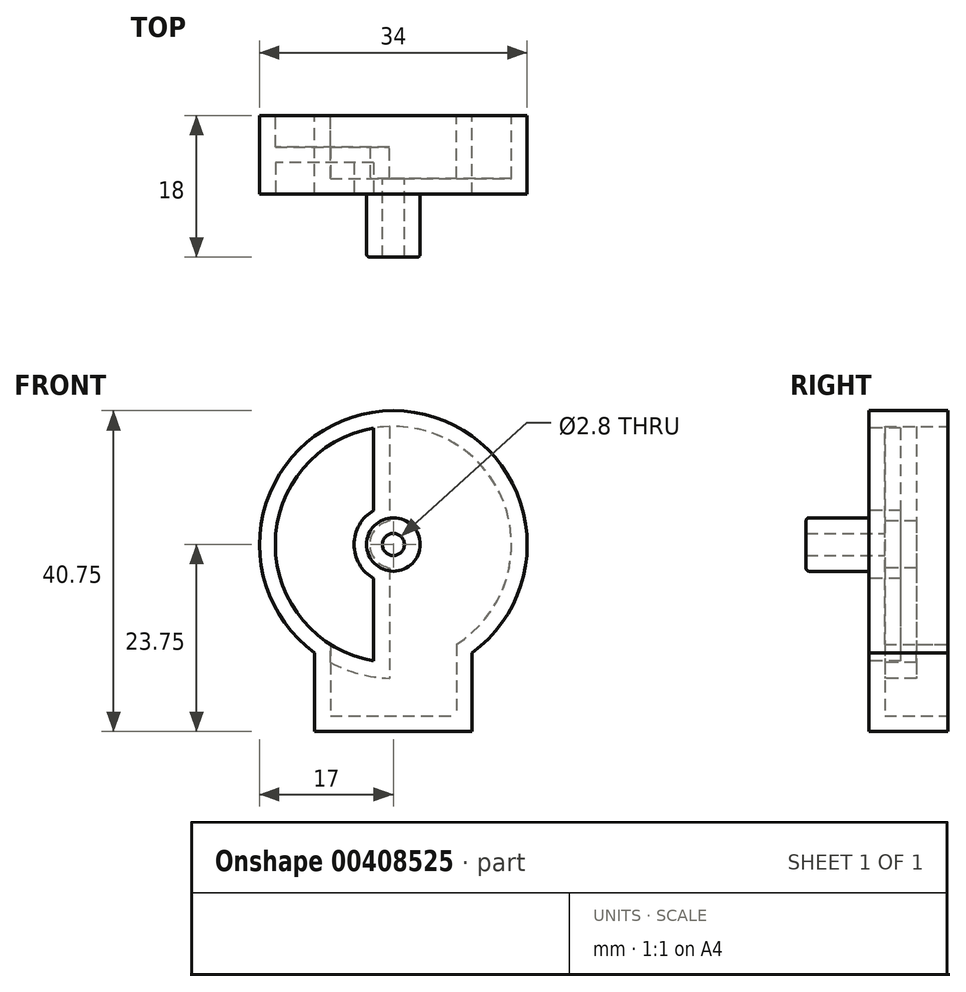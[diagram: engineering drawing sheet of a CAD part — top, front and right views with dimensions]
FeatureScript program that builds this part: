
annotation { "Feature Type Name" : "Feature", "Feature Type Description" : "" }
export const myFeature = defineFeature(function(context is Context, id is Id, definition is map)
    precondition{}
    {
        {
            var Q0;
            Q0=qCreatedBy(makeId("Front.planeOp"),FACE);
            var sketch = newSketch(context, id + "F0", { "sketchPlane" : qUnion([Q0])});
            skCircle(sketch, "E0", {"center": v(0, 0) * mm, "radius": 17 * mm});
            skLineSegment(sketch, "E1.bottom", {"start": v(-10, -13.75) * mm, "end": v(10, -13.75) * mm, "construction": true});
            skLineSegment(sketch, "E1.top", {"start": v(-10, -23.75) * mm, "end": v(10, -23.75) * mm});
            skLineSegment(sketch, "E1.left", {"start": v(-10, -13.75) * mm, "end": v(-10, -23.75) * mm});
            skLineSegment(sketch, "E1.right", {"start": v(10, -13.75) * mm, "end": v(10, -23.75) * mm});
            skLineSegment(sketch, "E2", {"start": v(0, 0) * mm, "end": v(0, -23.75) * mm, "construction": true});
            skPoint(sketch, "E3", {"position": v(0, -23.75) * mm});
            skSolve(sketch);
        }
        {
            var Q0;
            Q0=qSketchRegion(id+"F0",true);
            extrude(context, id + "F1", {"entities" : qUnion([Q0]), "depth" : 10 * mm});
        }
        {
            var Q0;
            Q0=makeQuery(id+"F1.opExtrude","CAP_FACE",FACE,{"disambiguationData":[OSD([sQuery(id+"F0.wireOp",EDGE,"E0"),sQuery(id+"F0.wireOp",EDGE,"E1.top"),sQuery(id+"F0.wireOp",EDGE,"E1.left"),sQuery(id+"F0.wireOp",EDGE,"E1.right")])],"isStart":false});
            var sketch = newSketch(context, id + "F2", { "sketchPlane" : qUnion([Q0])});
            skCircle(sketch, "E4", {"center": v(0, 0) * mm, "radius": 15 * mm, "construction": true});
            skCircle(sketch, "E5", {"center": v(0, 0) * mm, "radius": 5 * mm, "construction": true});
            skLineSegment(sketch, "E6", {"start": v(0, 15) * mm, "end": v(0, -15) * mm, "construction": true});
            skArc(sketch, "E7", {"start": v(-2.5, 14.8) * mm, "mid": v(-15, 0) * mm, "end": v(-2.5, -14.8) * mm});
            skArc(sketch, "E8", {"start": v(-2.5, 4.33) * mm, "mid": v(-5, 0) * mm, "end": v(-2.5, -4.33) * mm});
            skLineSegment(sketch, "E9", {"start": v(-2.5, 14.8) * mm, "end": v(-2.5, -14.8) * mm, "construction": true});
            skLineSegment(sketch, "E10", {"start": v(-2.5, -4.33) * mm, "end": v(-2.5, -14.8) * mm});
            skLineSegment(sketch, "E11", {"start": v(-2.5, 14.8) * mm, "end": v(-2.5, 4.33) * mm});
            skSolve(sketch);
        }
        {
            var Q0;
            Q0=qSketchRegion(id+"F2",true);
            extrude(context, id + "F3", {"entities" : qUnion([Q0]), "operationType" : NewBodyOperationType.REMOVE, "oppositeDirection" : true, "depth" : 4 * mm});
        }
        {
            var Q0;
            Q0=makeQuery(id+"F1.opExtrude","CAP_FACE",FACE,{"disambiguationData":[OSD([sQuery(id+"F0.wireOp",EDGE,"E0"),sQuery(id+"F0.wireOp",EDGE,"E1.top"),sQuery(id+"F0.wireOp",EDGE,"E1.left"),sQuery(id+"F0.wireOp",EDGE,"E1.right")])],"isStart":false});
            var sketch = newSketch(context, id + "F4", { "sketchPlane" : qUnion([Q0])});
            skCircle(sketch, "E12", {"center": v(0, 0) * mm, "radius": 3.4 * mm});
            skSolve(sketch);
        }
        {
            var Q0;
            Q0=qSketchRegion(id+"F4",true);
            extrude(context, id + "F5", {"entities" : qUnion([Q0]), "operationType" : NewBodyOperationType.ADD, "depth" : 8 * mm});
        }
        {
            var Q0;
            Q0=makeQuery(id+"F1.opExtrude","CAP_FACE",FACE,{"disambiguationData":[OSD([sQuery(id+"F0.wireOp",EDGE,"E0"),sQuery(id+"F0.wireOp",EDGE,"E1.top"),sQuery(id+"F0.wireOp",EDGE,"E1.left"),sQuery(id+"F0.wireOp",EDGE,"E1.right")])],"isStart":true});
            shell(context, id + "F6", {"entities" : qUnion([Q0]), "thickness" : 2 * mm});
        }
        {
            var Q0;
            Q0=makeQuery(id+"F5.opExtrude","CAP_EDGE",EDGE,{"disambiguationData":[OSD([sQuery(id+"F4.wireOp",EDGE,"E12")])],"isStart":true});
            var Q1;
            Q1=makeQuery(id+"F5.opExtrude","CAP_EDGE",EDGE,{"disambiguationData":[OSD([sQuery(id+"F4.wireOp",EDGE,"E12")])],"isStart":false});
            fillet(context, id + "F7", {"entities" : qUnion([Q0, Q1]), "radius" : .4 * mm, "tangentPropagation" : true, "allowEdgeOverflow" : false});
        }
        {
            var Q0;
            {var subQ0=sQuery(id+"F4.wireOp",EDGE,"E12");Q0=makeQuery(id+"F6.opShell","OFFSET_FACE",FACE,{"disambiguationData":[OSD([subQ0]),TDD([makeQuery(id+"F5.opExtrude","CAP_FACE",FACE,{"disambiguationData":[OSD([subQ0])],"isStart":false})])]});}
            extrude(context, id + "F9", {"entities" : qUnion([Q0]), "operationType" : NewBodyOperationType.REMOVE, "oppositeDirection" : true, "depth" : 25 * mm});
        }
    });
